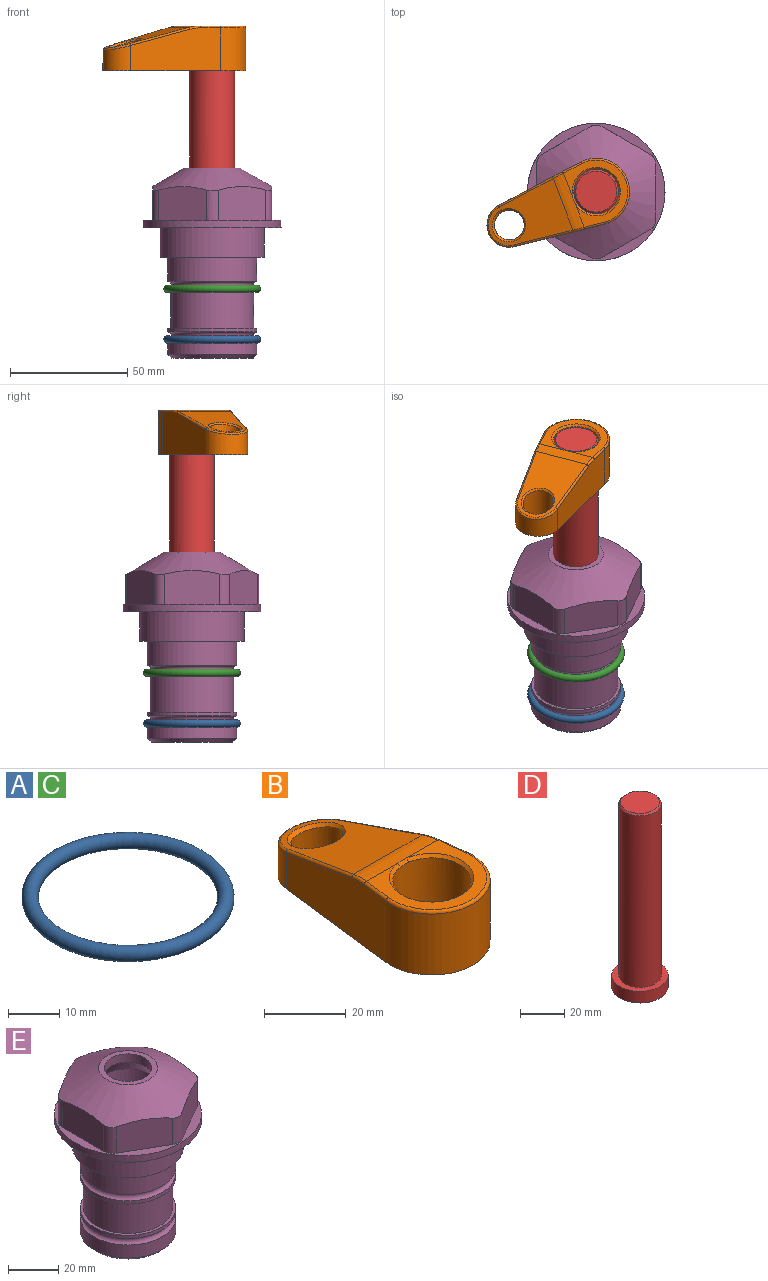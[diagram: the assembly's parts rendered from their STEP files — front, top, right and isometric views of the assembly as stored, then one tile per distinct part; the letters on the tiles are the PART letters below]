
ASSEMBLY  parts=5 mates=4
PART A: 1 faces, bbox 44.7x44.7x3.2 mm
  f0: torus R=19.05mm, axis (0,0,1), area 1193.9mm2
PART B: 31 faces, bbox 31.7x65.5x19.8 mm
  f0: plane 39.12x18.26mm, normal (0.99,0.12,0), area 612.2mm2, adj f1,f4,f7,f11,f13,f15
  f1: cylinder r=9.53mm len=18.91mm, axis (0,0,-1), area 296.1mm2, adj f0,f2,f7,f17
  f2: plane 39.12x18.26mm, normal (-0.99,0.12,0), area 612.2mm2, adj f1,f4,f7,f12,f14,f16
  f3: cylinder r=6.35mm len=12.7mm, axis (0,0,-1), area 362.4mm2, adj f7,f18
  f4: cylinder r=14.29mm len=28.58mm, axis (0,0,-1), area 882.2mm2, adj f0,f2,f7,f10
  f5: cylinder r=9.53mm len=19.05mm, axis (0,0,-1), area 1092.6mm2, adj f7,f19,f20
  f6: plane 26.99x23.69mm, normal (0,0,1), area 216.2mm2, adj f9,f10,f11,f12,f19
  f7: plane 63.5x28.58mm, normal (0,0,-1), area 661.8mm2, adj f0,f1,f2,f3,f4,f5,f22,f23
  f8: plane 33.52x23.6mm, normal (0,0.26,0.97), area 486mm2, adj f9,f15,f16,f17,f18
  f9: cylinder r=19.05mm len=24.72mm, axis (1,0,0), area 120.4mm2, adj f6,f8,f13,f14,f20
  f10: torus R=13.49mm, axis (0,0,1), area 59mm2, adj f4,f6,f11,f12
  f11: cylinder r=0.79mm len=8.67mm, axis (0.12,-0.99,0), area 10.8mm2, adj f0,f6,f10,f13
  f12: cylinder r=0.79mm len=8.67mm, axis (0.12,0.99,0), area 10.8mm2, adj f2,f6,f10,f14
  f13: bspline ~4.95x1.42mm, area 6.1mm2, adj f0,f9,f11,f15
  f14: bspline ~4.95x1.42mm, area 6.1mm2, adj f2,f9,f12,f16
  f15: cylinder r=0.79mm len=25.95mm, axis (0.12,-0.96,0.26), area 32.9mm2, adj f0,f8,f13,f17
  f16: cylinder r=0.79mm len=25.95mm, axis (0.12,0.96,-0.26), area 32.9mm2, adj f2,f8,f14,f17
  f17: bspline ~18.91x8.38mm, area 30mm2, adj f1,f8,f15,f16
  f18: bspline ~14.29x14.29mm, area 48.3mm2, adj f3,f8
  f19: cone r=9.53mm half-angle=45deg, axis (0,0,1), area 66.5mm2, adj f5,f6,f20
  f20: bspline ~3.22x0.96mm, area 3.5mm2, adj f5,f9,f19
  f21: plane 2.75x2.72mm, normal (0,0,-1), area 2.9mm2, adj f23,f25,f28
  f22: plane 23.05x15.88mm, normal (-0.99,-0.12,0), area 323.6mm2, adj f7,f25,f26,f27,f28,f29
  f23: plane 23.05x15.88mm, normal (0.99,-0.12,0), area 323.6mm2, adj f7,f21,f25,f27,f28,f30
  f24: cylinder r=9.53mm len=10.69mm, axis (0,0,-1), area 114.7mm2, adj f7,f27,f29,f30
  f25: cylinder r=12.7mm len=20.59mm, axis (0,0,-1), area 381.1mm2, adj f7,f21,f22,f23,f26,f28
  f26: plane 2.75x2.72mm, normal (0,0,-1), area 2.9mm2, adj f22,f25,f28
  f27: plane 19.72x18.37mm, normal (0,-0.26,-0.97), area 291.8mm2, adj f22,f23,f24,f28,f29,f30
  f28: cylinder r=15.88mm len=19.92mm, axis (1,0,0), area 54.8mm2, adj f21,f22,f23,f25,f26,f27
  f29: cylinder r=1.59mm len=11mm, axis (0,0,-1), area 34.7mm2, adj f7,f22,f24,f27
  f30: cylinder r=1.59mm len=11mm, axis (0,0,-1), area 34.7mm2, adj f7,f23,f24,f27
PART C: same geometry as A
PART D: 6 faces, bbox 25.4x25.4x101.6 mm
  f0: plane 17.46x17.46mm, normal (0,0,1), area 239.5mm2, adj f5
  f1: plane 25.4x25.4mm, normal (0,0,-1), area 506.7mm2, adj f2
  f2: cylinder r=12.7mm len=25.4mm, axis (0,0,1), area 506.7mm2, adj f1,f3
  f3: plane 25.4x25.4mm, normal (0,0,1), area 221.7mm2, adj f2,f4
  f4: cylinder r=9.53mm len=94.46mm, axis (0,0,1), area 5653mm2, adj f3,f5
  f5: cone r=8.73mm half-angle=45deg, axis (0,0,-1), area 64.4mm2, adj f0,f4
PART E: 36 faces, bbox 58.7x58.7x81 mm
  f0: cylinder r=17.78mm len=35.56mm, axis (0,0,1), area 1670.8mm2, adj f23,f24,f31
  f1: cylinder r=19.05mm len=38.1mm, axis (0,0,1), area 1191.9mm2, adj f26,f27,f30
  f2: plane 58.66x58.66mm, normal (0,0,-1), area 1150.6mm2, adj f3,f28
  f3: cylinder r=29.33mm len=58.66mm, axis (0,0,-1), area 585.1mm2, adj f2,f4
  f4: plane 58.66x58.66mm, normal (0,0,1), area 475.9mm2, adj f3,f5,f6,f7,f8,f9,f10,f11
  f5: plane 20.32x14.34mm, normal (-0.5,0.87,0), area 324.4mm2, adj f4,f15,f16,f17
  f6: plane 20.32x14.34mm, normal (0.5,0.87,0), area 324.4mm2, adj f4,f14,f15,f17
  f7: plane 23.48x14.34mm, normal (1,0,0), area 324.4mm2, adj f4,f13,f14,f17
  f8: plane 20.32x14.34mm, normal (0.5,-0.87,0), area 324.4mm2, adj f4,f12,f13,f17
  f9: plane 20.32x14.34mm, normal (-0.5,-0.87,0), area 324.4mm2, adj f4,f11,f12,f17
  f10: plane 23.48x14.34mm, normal (-1,0,0), area 324.4mm2, adj f4,f11,f16,f17
  f11: cylinder r=5.08mm len=12.85mm, axis (0,0,-1), area 67.2mm2, adj f4,f9,f10,f17
  f12: cylinder r=5.08mm len=12.85mm, axis (0,0,-1), area 67.2mm2, adj f4,f8,f9,f17
  f13: cylinder r=5.08mm len=12.85mm, axis (0,0,-1), area 67.2mm2, adj f4,f7,f8,f17
  f14: cylinder r=5.08mm len=12.85mm, axis (0,0,-1), area 67.2mm2, adj f4,f6,f7,f17
  f15: cylinder r=5.08mm len=12.85mm, axis (0,0,-1), area 67.2mm2, adj f4,f5,f6,f17
  f16: cylinder r=5.08mm len=12.85mm, axis (0,0,-1), area 67.2mm2, adj f4,f5,f10,f17
  f17: cone r=11.73mm half-angle=60deg, axis (0,0,-1), area 2071.8mm2, adj f5,f6,f7,f8,f9,f10,f11,f12
  f18: plane 23.46x23.46mm, normal (0,0,1), area 147.4mm2, adj f17,f35
  f19: plane 34.93x34.93mm, normal (0,0,-1), area 958mm2, adj f29
  f20: cylinder r=19.05mm len=38.1mm, axis (0,0,1), area 760.1mm2, adj f21,f29
  f21: torus R=19.05mm, axis (0,0,1), area 565.3mm2, adj f20,f22
  f22: cylinder r=19.05mm len=38.1mm, axis (0,0,1), area 190mm2, adj f21,f23
  f23: plane 38.1x38.1mm, normal (0,0,1), area 146.9mm2, adj f0,f22
  f24: plane 38.1x38.1mm, normal (0,0,-1), area 146.9mm2, adj f0,f25
  f25: cylinder r=19.05mm len=38.1mm, axis (0,0,1), area 190mm2, adj f24,f26
  f26: torus R=19.05mm, axis (0,0,1), area 565.3mm2, adj f1,f25
  f27: plane 44.45x44.45mm, normal (0,0,-1), area 411.7mm2, adj f1,f28
  f28: cylinder r=22.23mm len=44.45mm, axis (0,0,1), area 1773.5mm2, adj f2,f27
  f29: cone r=19.05mm half-angle=45deg, axis (0,0,1), area 257.5mm2, adj f19,f20
  f30: cylinder r=3.17mm len=6.75mm, axis (-1,0,0), area 128mm2, adj f1,f33
  f31: cylinder r=3.17mm len=6.35mm, axis (-1,0,0), area 102.5mm2, adj f0,f33
  f32: plane 25.4x25.4mm, normal (0,0,1), area 506.7mm2, adj f33
  f33: cylinder r=12.7mm len=66.42mm, axis (0,0,-1), area 5236.2mm2, adj f30,f31,f32,f34
  f34: cone r=9.53mm half-angle=30deg, axis (0,0,-1), area 443.4mm2, adj f33,f35
  f35: cylinder r=9.53mm len=19.05mm, axis (0,0,-1), area 240.9mm2, adj f18,f34
PLACE A t=(0,0,-23.18)mm
PLACE B rot(axis=(0,0,1),111deg) t=(0,0,22.46)mm
PLACE C t=(0,0,-1.59)mm
PLACE D rot(axis=(0,0,1),111deg) t=(0,0,21.67)mm
PLACE E at identity fixed
MATE fastened C.f0 <-> E.f0  axis (0,0,1) through (0,0,-26.1)mm
MATE fastened A.f0 <-> E.f0  axis (0,0,1) through (0,0,-47.69)mm
MATE fastened D.f2 <-> B.f4  axis (0,0,1) through (0,0,85.17)mm
MATE cylindrical D.f2 <-> E.f0  axis (0,0,-1) through (0,0,-16.43)mm
